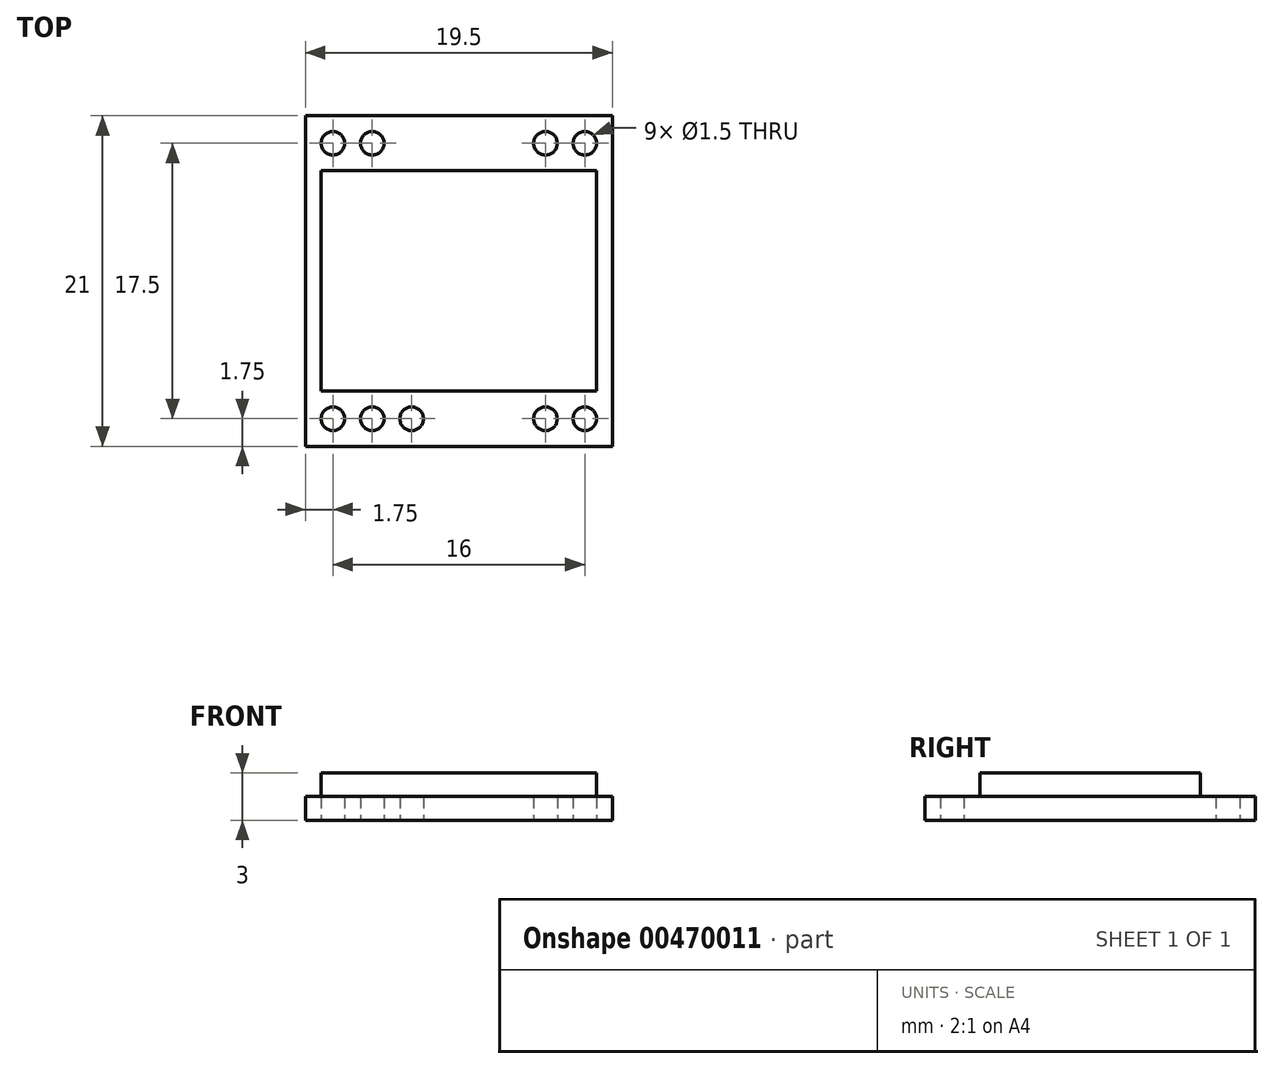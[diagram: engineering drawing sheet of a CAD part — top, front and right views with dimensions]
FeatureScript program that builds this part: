
annotation { "Feature Type Name" : "Feature", "Feature Type Description" : "" }
export const myFeature = defineFeature(function(context is Context, id is Id, definition is map)
    precondition{}
    {
        {
            var Q0;
            Q0=qCreatedBy(makeId("Top.planeOp"),FACE);
            var sketch = newSketch(context, id + "F0", { "sketchPlane" : qUnion([Q0])});
            skLineSegment(sketch, "E0.bottom", {"start": v(9.75, -10.5) * mm, "end": v(-9.75, -10.5) * mm});
            skLineSegment(sketch, "E0.top", {"start": v(9.75, 10.5) * mm, "end": v(-9.75, 10.5) * mm});
            skLineSegment(sketch, "E0.left", {"start": v(9.75, -10.5) * mm, "end": v(9.75, 10.5) * mm});
            skLineSegment(sketch, "E0.right", {"start": v(-9.75, -10.5) * mm, "end": v(-9.75, 10.5) * mm});
            skPoint(sketch, "E0.middle", {"position": v(0, 0) * mm});
            skCircle(sketch, "E1", {"center": v(-8, -8.75) * mm, "radius": 0.75 * mm});
            skCircle(sketch, "E2", {"center": v(-5.5, -8.75) * mm, "radius": 0.75 * mm});
            skCircle(sketch, "E3", {"center": v(-3, -8.75) * mm, "radius": 0.75 * mm});
            skCircle(sketch, "E4.MirrorC", {"center": v(5.5, -8.75) * mm, "radius": 0.75 * mm});
            skCircle(sketch, "E5.MirrorC", {"center": v(8, -8.75) * mm, "radius": 0.75 * mm});
            skCircle(sketch, "E6.MirrorC", {"center": v(-8, 8.75) * mm, "radius": 0.75 * mm});
            skCircle(sketch, "E7.MirrorC", {"center": v(-5.5, 8.75) * mm, "radius": 0.75 * mm});
            skCircle(sketch, "E8.MirrorC", {"center": v(5.5, 8.75) * mm, "radius": 0.75 * mm});
            skCircle(sketch, "E9.MirrorC", {"center": v(8, 8.75) * mm, "radius": 0.75 * mm});
            skLineSegment(sketch, "E10.bottom", {"start": v(8.75, -7) * mm, "end": v(-8.75, -7) * mm});
            skLineSegment(sketch, "E10.top", {"start": v(8.75, 7) * mm, "end": v(-8.75, 7) * mm});
            skLineSegment(sketch, "E10.left", {"start": v(8.75, -7) * mm, "end": v(8.75, 7) * mm});
            skLineSegment(sketch, "E10.right", {"start": v(-8.75, -7) * mm, "end": v(-8.75, 7) * mm});
            skSolve(sketch);
        }
        {
            var Q0;
            Q0 = qSketchRegion(id + "F0", true);
            extrude(context, id + "F1", {"entities" : qUnion([Q0]), "depth" : 1.5 * mm, "offsetDistance" : 25 * mm});
        }
        {
            var Q0;
            Q0=makeQuery(id+"F0.imprint","IMPRINT",FACE,{"disambiguationData":[TD([[makeQuery(id+"F0.imprint","IMPRINT",EDGE,{"derivedFrom":sQuery(id+"F0.wireOp",EDGE,"E10.bottom")}),-1.0]])]});
            extrude(context, id + "F2", {"entities" : qUnion([Q0]), "operationType" : NewBodyOperationType.ADD, "depth" : 3 * mm, "offsetDistance" : 25 * mm});
        }
    });
